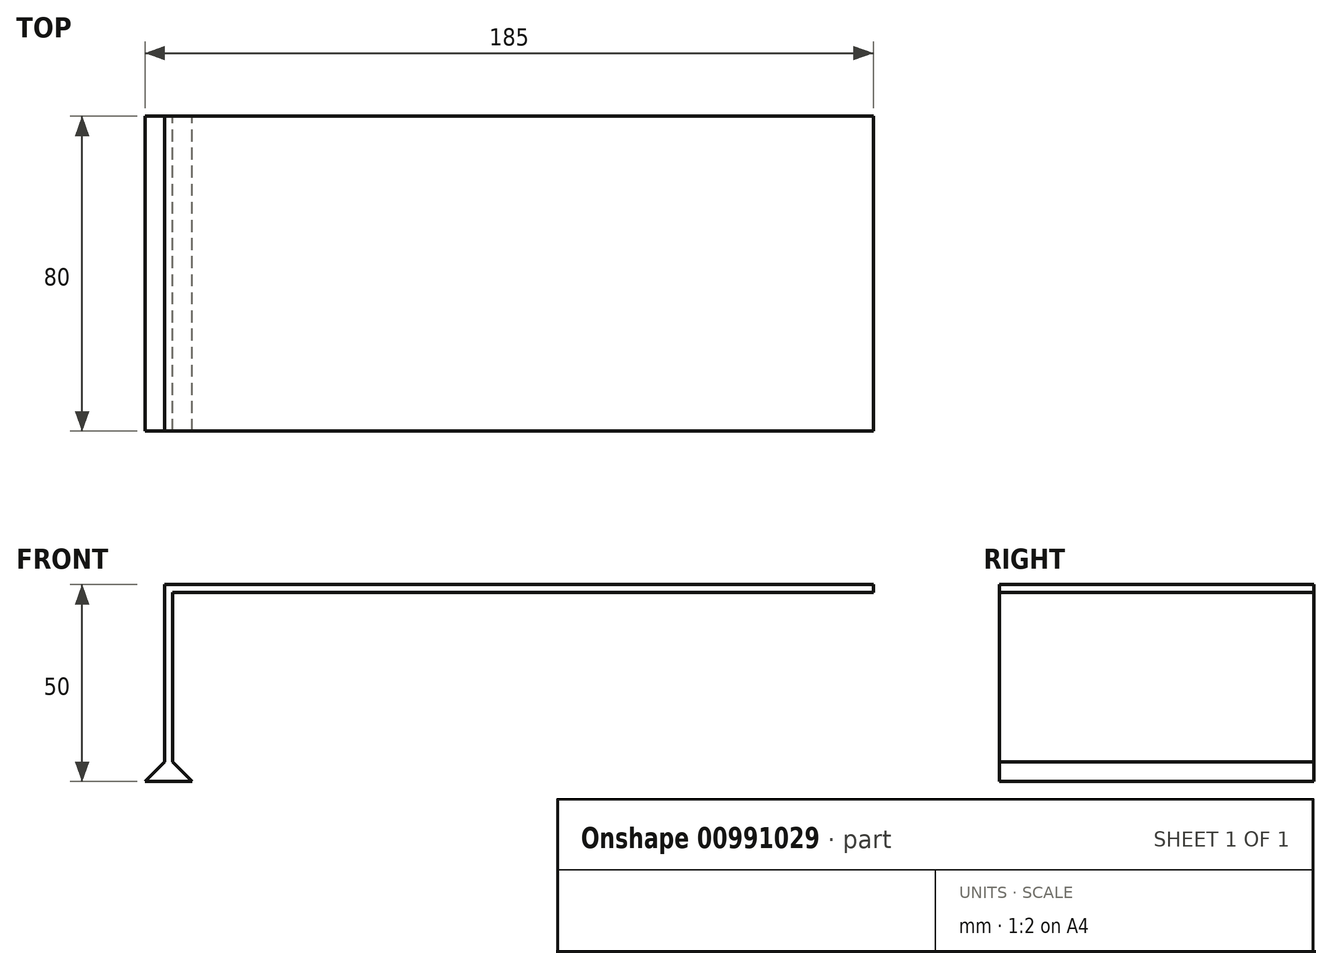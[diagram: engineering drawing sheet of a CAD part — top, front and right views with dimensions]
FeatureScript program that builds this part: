
annotation { "Feature Type Name" : "Feature", "Feature Type Description" : "" }
export const myFeature = defineFeature(function(context is Context, id is Id, definition is map)
    precondition{}
    {
        {
            var Q0;
            Q0=qCreatedBy(makeId("Front.planeOp"),FACE);
            var sketch = newSketch(context, id + "F0", { "sketchPlane" : qUnion([Q0])});
            skLineSegment(sketch, "E0", {"start": v(-39.1, 0) * mm, "end": v(-39.1, 48) * mm});
            skLineSegment(sketch, "E1", {"start": v(-39.1, 48) * mm, "end": v(138.9, 48) * mm});
            skLineSegment(sketch, "E2", {"start": v(138.9, 48) * mm, "end": v(138.9, 50) * mm});
            skLineSegment(sketch, "E3", {"start": v(138.9, 50) * mm, "end": v(-41.1, 50) * mm});
            skLineSegment(sketch, "E4", {"start": v(-41.1, 50) * mm, "end": v(-41.1, 0) * mm});
            skLineSegment(sketch, "E5", {"start": v(-41.1, 0) * mm, "end": v(-39.1, 0) * mm});
            skLineSegment(sketch, "E6", {"start": v(-41.1, 5) * mm, "end": v(-46.1, 0) * mm});
            skLineSegment(sketch, "E7", {"start": v(-46.1, 0) * mm, "end": v(-41.1, 0) * mm});
            skLineSegment(sketch, "E8", {"start": v(-39.1, 5) * mm, "end": v(-34.1, 0) * mm});
            skLineSegment(sketch, "E9", {"start": v(-34.1, 0) * mm, "end": v(-39.1, 0) * mm});
            skSolve(sketch);
        }
        {
            var Q0;
            Q0 = qSketchRegion(id + "F0", true);
            extrude(context, id + "F1", {"entities" : qUnion([Q0]), "endBound" : BoundingType.SYMMETRIC, "depth" : 80 * mm, "offsetDistance" : 25 * mm});
        }
    });
